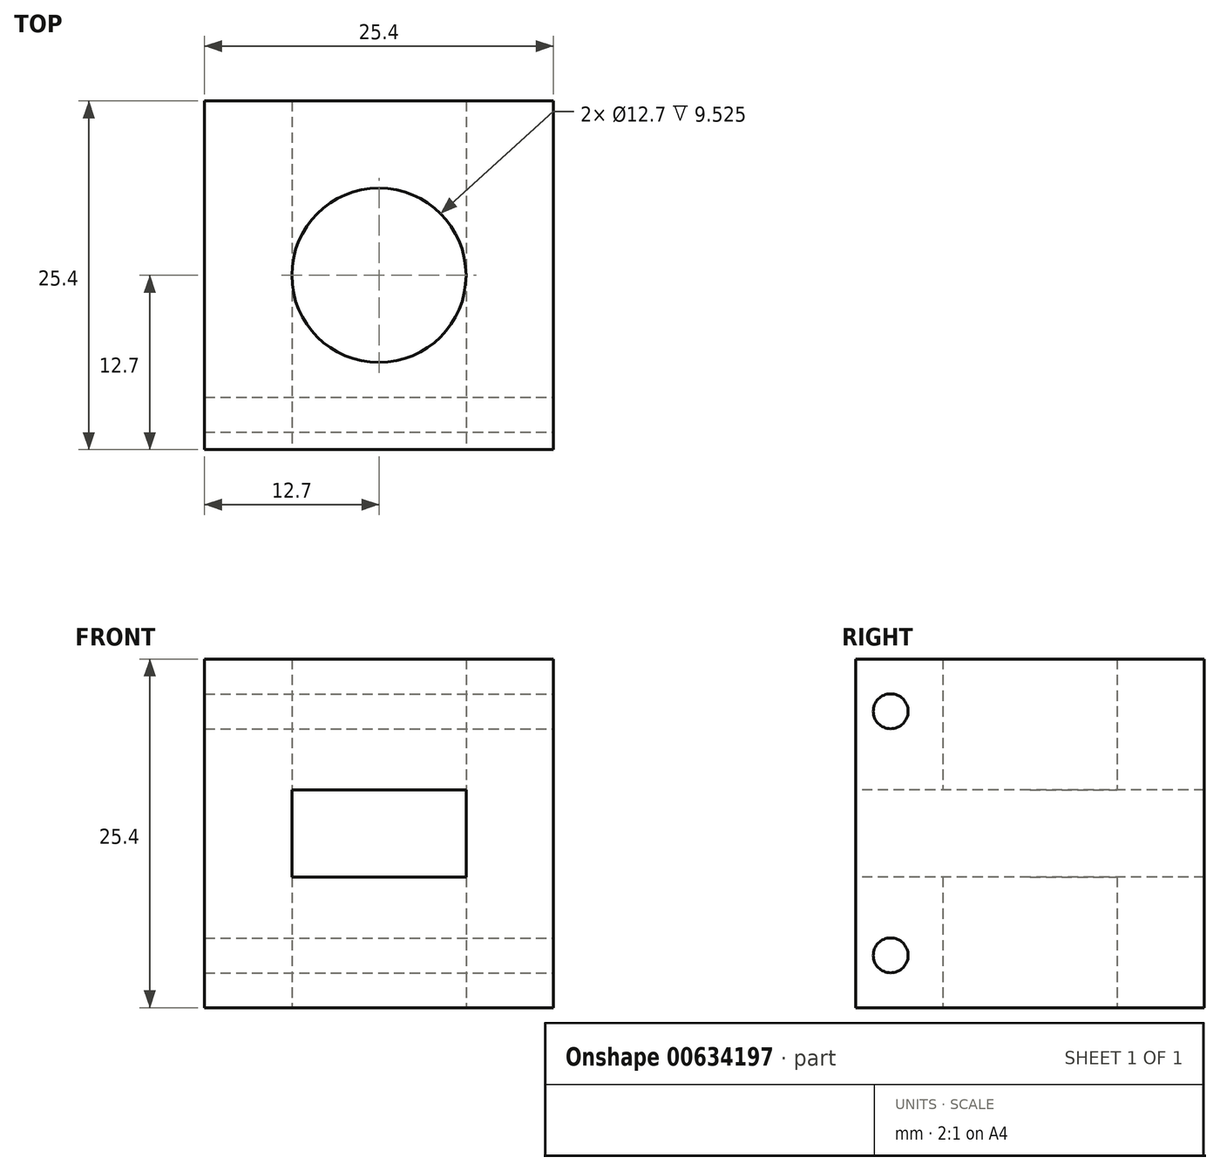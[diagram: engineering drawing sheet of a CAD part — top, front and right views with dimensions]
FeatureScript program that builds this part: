
annotation { "Feature Type Name" : "Feature", "Feature Type Description" : "" }
export const myFeature = defineFeature(function(context is Context, id is Id, definition is map)
    precondition{}
    {
        {
            var Q0;
            Q0=qCreatedBy(makeId("Top.planeOp"),FACE);
            var sketch = newSketch(context, id + "F0", { "sketchPlane" : qUnion([Q0])});
            skLineSegment(sketch, "E0.bottom", {"start": v(0, 0) * mm, "end": v(-25.4, 0) * mm});
            skLineSegment(sketch, "E0.top", {"start": v(0, 25.4) * mm, "end": v(-25.4, 25.4) * mm});
            skLineSegment(sketch, "E0.left", {"start": v(0, 0) * mm, "end": v(0, 25.4) * mm});
            skLineSegment(sketch, "E0.right", {"start": v(-25.4, 0) * mm, "end": v(-25.4, 25.4) * mm});
            skLineSegment(sketch, "E1", {"start": v(-12.7, 25.4) * mm, "end": v(-12.7, 12.7) * mm});
            skCircle(sketch, "E2", {"center": v(-12.7, 12.7) * mm, "radius": 6.35 * mm});
            skLineSegment(sketch, "E3.bottom", {"start": v(-25.4, 0) * mm, "end": v(-21.59, 0) * mm});
            skLineSegment(sketch, "E3.left", {"start": v(-25.4, 0) * mm, "end": v(-25.4, 2.54) * mm});
            skLineSegment(sketch, "E4.bottom", {"start": v(0, 0) * mm, "end": v(-3.8, 0) * mm});
            skLineSegment(sketch, "E4.left", {"start": v(0, 0) * mm, "end": v(0, 2.54) * mm});
            skSolve(sketch);
        }
        {
            var Q0;
            Q0=makeQuery(id+"F0.imprint","IMPRINT",FACE,{"disambiguationData":[TD([[makeQuery(id+"F0.imprint","IMPRINT",EDGE,{"derivedFrom":sQuery(id+"F0.wireOp",EDGE,"E0.bottom")}),-1.0]])]});
            extrude(context, id + "F1", {"entities" : qUnion([Q0]), "depth" : 25.4 * mm, "offsetDistance" : 25.4 * mm});
        }
        {
            var Q0;
            Q0=makeQuery(id+"F1.opExtrude","SWEPT_FACE",FACE,{"disambiguationData":[OSD([sQuery(id+"F0.wireOp",EDGE,"E0.bottom")])]});
            var sketch = newSketch(context, id + "F2", { "sketchPlane" : qUnion([Q0])});
            skLineSegment(sketch, "E5.bottom", {"start": v(-19.05, 15.88) * mm, "end": v(-6.35, 15.88) * mm});
            skLineSegment(sketch, "E5.top", {"start": v(-19.05, 9.52) * mm, "end": v(-6.35, 9.52) * mm});
            skLineSegment(sketch, "E5.left", {"start": v(-19.05, 15.88) * mm, "end": v(-19.05, 9.52) * mm});
            skLineSegment(sketch, "E5.right", {"start": v(-6.35, 15.88) * mm, "end": v(-6.35, 9.52) * mm});
            skPoint(sketch, "E5.middle", {"position": v(-12.7, 12.7) * mm});
            skPoint(sketch, "E6.start.orphan", {"position": v(-12.7, 25.4) * mm});
            skSolve(sketch);
        }
        {
            var Q0;
            Q0=makeQuery(id+"F2.imprint","IMPRINT",FACE,{"disambiguationData":[TD([[makeQuery(id+"F2.imprint","IMPRINT",EDGE,{"derivedFrom":sQuery(id+"F2.wireOp",EDGE,"sCiIrLAm-vf3y-ts9W-TCKf-l6HsWwnXEy8x")}),1.0]])]});
            var Q1;
            Q1=makeQuery(id+"F2.imprint","IMPRINT",FACE,{"disambiguationData":[TD([[makeQuery(id+"F2.imprint","IMPRINT",EDGE,{"derivedFrom":sQuery(id+"F2.wireOp",EDGE,"E5.bottom")}),-1.0]])]});
            extrude(context, id + "F3", {"entities" : qUnion([Q0, Q1]), "operationType" : NewBodyOperationType.REMOVE, "oppositeDirection" : true, "depth" : 25.4 * mm, "offsetDistance" : 25.4 * mm});
        }
        {
            var Q0;
            Q0=makeQuery(id+"F1.opExtrude","SWEPT_FACE",FACE,{"disambiguationData":[OSD([sQuery(id+"F0.wireOp",EDGE,"E0.left"),sQuery(id+"F0.wireOp",EDGE,"E4.left")])]});
            var sketch = newSketch(context, id + "F4", { "sketchPlane" : qUnion([Q0])});
            skLineSegment(sketch, "E7.bottom", {"start": v(0, 25.4) * mm, "end": v(2.54, 25.4) * mm});
            skLineSegment(sketch, "E7.top", {"start": v(0, 21.59) * mm, "end": v(2.54, 21.59) * mm});
            skLineSegment(sketch, "E7.left", {"start": v(0, 25.4) * mm, "end": v(0, 21.59) * mm});
            skLineSegment(sketch, "E7.right", {"start": v(2.54, 25.4) * mm, "end": v(2.54, 21.59) * mm});
            skLineSegment(sketch, "E8.bottom", {"start": v(0, 0) * mm, "end": v(2.54, 0) * mm});
            skLineSegment(sketch, "E8.top", {"start": v(0, 3.81) * mm, "end": v(2.54, 3.81) * mm});
            skLineSegment(sketch, "E8.left", {"start": v(0, 0) * mm, "end": v(0, 3.81) * mm});
            skLineSegment(sketch, "E8.right", {"start": v(2.54, 0) * mm, "end": v(2.54, 3.81) * mm});
            skCircle(sketch, "E9", {"center": v(2.54, 21.59) * mm, "radius": 1.27 * mm});
            skCircle(sketch, "E10", {"center": v(2.54, 3.81) * mm, "radius": 1.27 * mm});
            skSolve(sketch);
        }
        {
            var Q0;
            {var subQ0=sQuery(id+"F4.wireOp",EDGE,"E7.right");var subQ1=sQuery(id+"F4.wireOp",EDGE,"E7.top");var subQ2=makeQuery(id+"F4.imprint","INTERSECT",VERTEX,{"derivedFrom":[subQ1,subQ0]});Q0=makeQuery(id+"F4.imprint","IMPRINT",FACE,{"disambiguationData":[TD([[makeQuery(id+"F4.imprint","IMPRINT",EDGE,{"disambiguationData":[TD([[subQ2,1.0]])],"derivedFrom":subQ1}),-1.0]])]});}
            var Q1;
            {var subQ0=sQuery(id+"F4.wireOp",EDGE,"E7.right");var subQ1=sQuery(id+"F4.wireOp",EDGE,"E7.top");var subQ2=makeQuery(id+"F4.imprint","INTERSECT",VERTEX,{"derivedFrom":[subQ1,subQ0]});Q1=makeQuery(id+"F4.imprint","IMPRINT",FACE,{"disambiguationData":[TD([[makeQuery(id+"F4.imprint","IMPRINT",EDGE,{"disambiguationData":[TD([[subQ2,1.0]])],"derivedFrom":subQ1}),1.0]])]});}
            var Q2;
            {var subQ0=sQuery(id+"F4.wireOp",EDGE,"E8.right");var subQ1=sQuery(id+"F4.wireOp",EDGE,"E8.top");var subQ2=makeQuery(id+"F4.imprint","INTERSECT",VERTEX,{"derivedFrom":[subQ1,subQ0]});Q2=makeQuery(id+"F4.imprint","IMPRINT",FACE,{"disambiguationData":[TD([[makeQuery(id+"F4.imprint","IMPRINT",EDGE,{"disambiguationData":[TD([[subQ2,1.0]])],"derivedFrom":subQ1}),1.0]])]});}
            var Q3;
            {var subQ0=sQuery(id+"F4.wireOp",EDGE,"E8.right");var subQ1=sQuery(id+"F4.wireOp",EDGE,"E8.top");var subQ2=makeQuery(id+"F4.imprint","INTERSECT",VERTEX,{"derivedFrom":[subQ1,subQ0]});Q3=makeQuery(id+"F4.imprint","IMPRINT",FACE,{"disambiguationData":[TD([[makeQuery(id+"F4.imprint","IMPRINT",EDGE,{"disambiguationData":[TD([[subQ2,1.0]])],"derivedFrom":subQ1}),-1.0]])]});}
            extrude(context, id + "F5", {"entities" : qUnion([Q0, Q1, Q2, Q3]), "operationType" : NewBodyOperationType.REMOVE, "oppositeDirection" : true, "depth" : 25.4 * mm, "offsetDistance" : 25.4 * mm});
        }
    });
